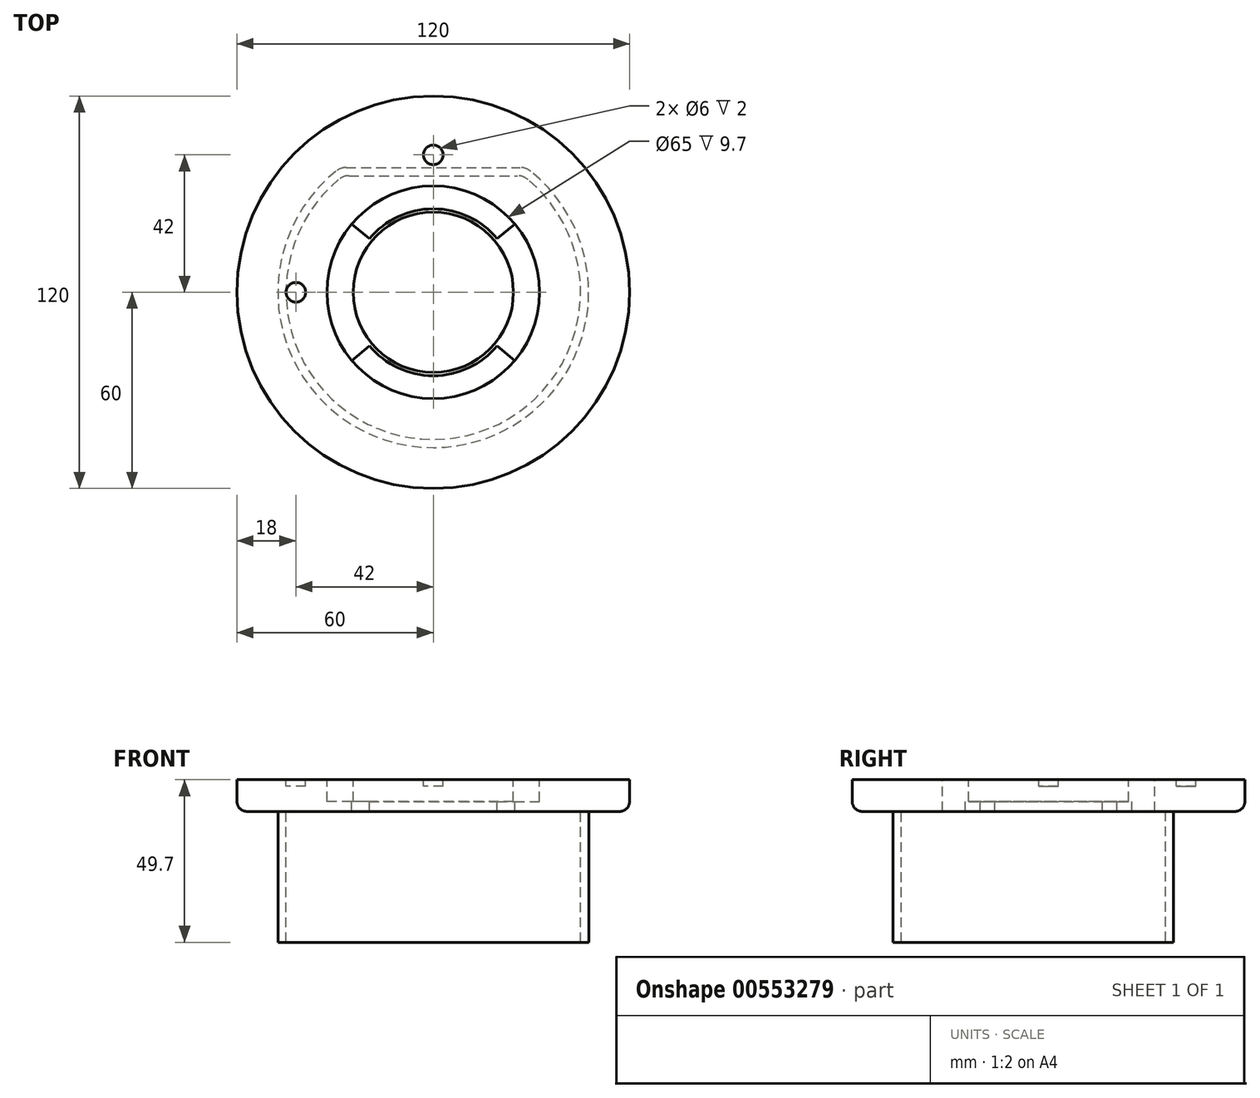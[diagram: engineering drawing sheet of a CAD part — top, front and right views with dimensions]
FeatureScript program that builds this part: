
annotation { "Feature Type Name" : "Feature", "Feature Type Description" : "" }
export const myFeature = defineFeature(function(context is Context, id is Id, definition is map)
    precondition{}
    {
        {
            var Q0;
            Q0=qCreatedBy(makeId("Top.planeOp"),FACE);
            var sketch = newSketch(context, id + "F0", { "sketchPlane" : qUnion([Q0])});
            skCircle(sketch, "E0", {"center": v(0, 0) * mm, "radius": 60 * mm});
            skSolve(sketch);
        }
        {
            var Q0;
            Q0 = qSketchRegion(id + "F0", true);
            extrude(context, id + "F1", {"entities" : qUnion([Q0]), "depth" : 9.7 * mm, "offsetDistance" : 25 * mm});
        }
        {
            var Q0;
            Q0=makeQuery(id+"F1.opExtrude","CAP_FACE",FACE,{"disambiguationData":[OSD([sQuery(id+"F0.wireOp",EDGE,"E0")])],"isStart":false});
            var sketch = newSketch(context, id + "F2", { "sketchPlane" : qUnion([Q0])});
            skCircle(sketch, "E1", {"center": v(0, 0) * mm, "radius": 32.5 * mm});
            skCircle(sketch, "E2", {"center": v(0, 0) * mm, "radius": 24.5 * mm});
            skSolve(sketch);
        }
        {
            var Q0;
            Q0=makeQuery(id+"F2.imprint","IMPRINT",FACE,{"disambiguationData":[TD([[makeQuery(id+"F2.imprint","IMPRINT",EDGE,{"derivedFrom":sQuery(id+"F2.wireOp",EDGE,"E1")}),1.0]])]});
            extrude(context, id + "F3", {"entities" : qUnion([Q0]), "operationType" : NewBodyOperationType.REMOVE, "oppositeDirection" : true, "depth" : 6.7 * mm, "offsetDistance" : 25 * mm});
        }
        {
            var Q0;
            Q0=makeQuery(id+"F3.boolean.opBoolean","COPY",FACE,{"derivedFrom":makeQuery(id+"F3.opExtrude","CAP_FACE",FACE,{"disambiguationData":[OSD([sQuery(id+"F2.wireOp",EDGE,"E1"),sQuery(id+"F2.wireOp",EDGE,"E2")])],"isStart":false})});
            var sketch = newSketch(context, id + "F4", { "sketchPlane" : qUnion([Q0])});
            skArc(sketch, "E3", {"start": v(19.53, 16.4) * mm, "mid": v(0, 25.5) * mm, "end": v(-19.53, 16.4) * mm});
            skLineSegment(sketch, "E4", {"start": v(19.53, 16.4) * mm, "end": v(24.9, 20.9) * mm});
            skLineSegment(sketch, "E5", {"start": v(-19.53, 16.4) * mm, "end": v(-24.9, 20.9) * mm});
            skLineSegment(sketch, "E6.MirrorCS", {"start": v(19.53, -16.4) * mm, "end": v(24.9, -20.9) * mm});
            skLineSegment(sketch, "E7.MirrorCS", {"start": v(-19.53, -16.4) * mm, "end": v(-24.9, -20.9) * mm});
            skArc(sketch, "E8.trimOffspring", {"start": v(-19.53, -16.4) * mm, "mid": v(0, -25.5) * mm, "end": v(19.53, -16.4) * mm});
            skSolve(sketch);
        }
        {
            var Q0;
            {var subQ0=sQuery(id+"F4.wireOp",EDGE,"E6.MirrorCS");Q0=makeQuery(id+"F4.imprint","IMPRINT",FACE,{"disambiguationData":[TD([[makeQuery(id+"F4.imprint","IMPRINT",EDGE,{"derivedFrom":subQ0}),-1.0]])]});}
            var Q1;
            Q1=makeQuery(id+"F4.imprint","IMPRINT",FACE,{"disambiguationData":[TD([[makeQuery(id+"F4.imprint","IMPRINT",EDGE,{"derivedFrom":sQuery(id+"F4.wireOp",EDGE,"E3")}),-1.0]])]});
            extrude(context, id + "F5", {"entities" : qUnion([Q0, Q1]), "operationType" : NewBodyOperationType.REMOVE, "endBound" : BoundingType.THROUGH_ALL, "oppositeDirection" : true, "depth" : 25 * mm, "offsetDistance" : 25 * mm});
        }
        {
            var Q0;
            Q0=makeQuery(id+"F1.opExtrude","CAP_FACE",FACE,{"disambiguationData":[OSD([sQuery(id+"F0.wireOp",EDGE,"E0")])],"isStart":true});
            var sketch = newSketch(context, id + "F6", { "sketchPlane" : qUnion([Q0])});
            skSolve(sketch);
        }
        {
            var Q0;
            {var subQ0=sQuery(id+"F0.wireOp",EDGE,"E0");Q0=makeQuery(id+"F3.boolean.opBoolean","SPLIT",FACE,{"disambiguationData":[TD([makeQuery(id+"F1.opExtrude","SWEPT_FACE",FACE,{"disambiguationData":[OSD([subQ0])]})])],"derivedFrom":makeQuery(id+"F1.opExtrude","CAP_FACE",FACE,{"disambiguationData":[OSD([subQ0])],"isStart":false})});}
            var sketch = newSketch(context, id + "F7", { "sketchPlane" : qUnion([Q0])});
            skCircle(sketch, "E9", {"center": v(0, 42) * mm, "radius": 3 * mm});
            skCircle(sketch, "E10", {"center": v(-42, 0) * mm, "radius": 3 * mm});
            skSolve(sketch);
        }
        {
            var Q0;
            Q0 = qSketchRegion(id + "F7", true);
            extrude(context, id + "F8", {"entities" : qUnion([Q0]), "operationType" : NewBodyOperationType.REMOVE, "oppositeDirection" : true, "depth" : 2 * mm, "offsetDistance" : 25 * mm});
        }
        {
            var Q0;
            {var subQ1=sQuery(id+"F0.wireOp",EDGE,"E0");Q0=makeQuery(id+"F6.imprint","IMPRINT",FACE,{"disambiguationData":[TD([[makeQuery(id+"F6.imprint","IMPRINT",EDGE,{"derivedFrom":makeQuery(id+"F1.opExtrude","CAP_EDGE",EDGE,{"disambiguationData":[OSD([subQ1])],"isStart":true})}),-1.0]])]});}
            var sketch = newSketch(context, id + "F9", { "sketchPlane" : qUnion([Q0])});
            skArc(sketch, "E11", {"start": v(27.5, -35.62) * mm, "mid": v(0, 45) * mm, "end": v(-27.5, -35.62) * mm});
            skArc(sketch, "E12", {"start": v(28.34, -38.12) * mm, "mid": v(0, 47.5) * mm, "end": v(-28.34, -38.12) * mm});
            skLineSegment(sketch, "E13", {"start": v(-27.5, -35.62) * mm, "end": v(27.5, -35.62) * mm});
            skLineSegment(sketch, "E14", {"start": v(-28.34, -38.12) * mm, "end": v(28.34, -38.12) * mm});
            skSolve(sketch);
        }
        {
            var Q0;
            Q0=makeQuery(id+"F9.imprint","IMPRINT",FACE,{"disambiguationData":[TD([[makeQuery(id+"F9.imprint","IMPRINT",EDGE,{"derivedFrom":sQuery(id+"F9.wireOp",EDGE,"E11")}),-1.0]])]});
            extrude(context, id + "F10", {"entities" : qUnion([Q0]), "operationType" : NewBodyOperationType.ADD, "depth" : 40 * mm, "offsetDistance" : 25 * mm});
        }
        {
            var Q0;
            Q0=makeQuery(id+"F1.opExtrude","CAP_EDGE",EDGE,{"disambiguationData":[OSD([sQuery(id+"F0.wireOp",EDGE,"E0")])],"isStart":true});
            fillet(context, id + "F11", {"entities" : qUnion([Q0]), "radius" : 3 * mm, "tangentPropagation" : true, "allowEdgeOverflow" : false});
        }
        {
            var Q0;
            {var subQ0=sQuery(id+"F9.wireOp",EDGE,"E13");var subQ1=sQuery(id+"F9.wireOp",EDGE,"E11");Q0=makeQuery(id+"F10.opExtrude","SWEPT_EDGE",EDGE,{"disambiguationData":[OSD([subQ1,subQ0]),TDD([makeQuery(id+"F9.imprint","INTERSECT",VERTEX,{"disambiguationData":[OD(0.0)],"derivedFrom":[subQ1,subQ0]})])]});}
            var Q1;
            {var subQ0=sQuery(id+"F9.wireOp",EDGE,"E13");var subQ1=sQuery(id+"F9.wireOp",EDGE,"E11");Q1=makeQuery(id+"F10.opExtrude","SWEPT_EDGE",EDGE,{"disambiguationData":[OSD([subQ1,subQ0]),TDD([makeQuery(id+"F9.imprint","INTERSECT",VERTEX,{"disambiguationData":[OD(1.0)],"derivedFrom":[subQ1,subQ0]})])]});}
            var Q2;
            {var subQ0=sQuery(id+"F9.wireOp",EDGE,"E14");var subQ1=sQuery(id+"F9.wireOp",EDGE,"E12");Q2=makeQuery(id+"F10.opExtrude","SWEPT_EDGE",EDGE,{"disambiguationData":[OSD([subQ1,subQ0]),TDD([makeQuery(id+"F9.imprint","INTERSECT",VERTEX,{"disambiguationData":[OD(1.0)],"derivedFrom":[subQ1,subQ0]})])]});}
            var Q3;
            {var subQ0=sQuery(id+"F9.wireOp",EDGE,"E14");var subQ1=sQuery(id+"F9.wireOp",EDGE,"E12");Q3=makeQuery(id+"F10.opExtrude","SWEPT_EDGE",EDGE,{"disambiguationData":[OSD([subQ1,subQ0]),TDD([makeQuery(id+"F9.imprint","INTERSECT",VERTEX,{"disambiguationData":[OD(0.0)],"derivedFrom":[subQ1,subQ0]})])]});}
            fillet(context, id + "F12", {"entities" : qUnion([Q0, Q1, Q2, Q3]), "radius" : 5 * mm, "tangentPropagation" : true, "allowEdgeOverflow" : false});
        }
    });
